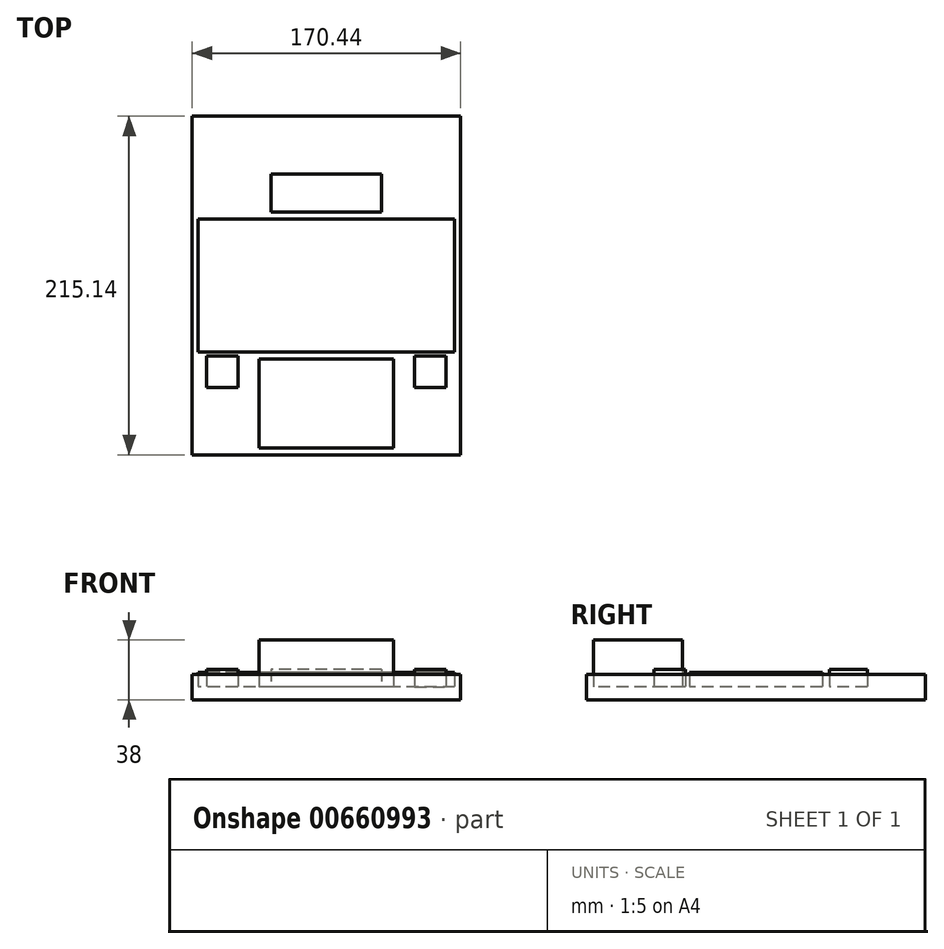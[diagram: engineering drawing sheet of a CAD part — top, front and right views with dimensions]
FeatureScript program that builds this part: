
annotation { "Feature Type Name" : "Feature", "Feature Type Description" : "" }
export const myFeature = defineFeature(function(context is Context, id is Id, definition is map)
    precondition{}
    {
        {
            var Q0;
            Q0=qCreatedBy(makeId("Top.planeOp"),FACE);
            var sketch = newSketch(context, id + "F0", { "sketchPlane" : qUnion([Q0])});
            skLineSegment(sketch, "E0.bottom", {"start": v(81.47, 42.2) * mm, "end": v(-81.47, 42.2) * mm});
            skLineSegment(sketch, "E0.top", {"start": v(81.47, -42.2) * mm, "end": v(-81.47, -42.2) * mm});
            skLineSegment(sketch, "E0.left", {"start": v(81.47, 42.2) * mm, "end": v(81.47, -42.2) * mm});
            skLineSegment(sketch, "E0.right", {"start": v(-81.47, 42.2) * mm, "end": v(-81.47, -42.2) * mm});
            skPoint(sketch, "E0.middle", {"position": v(0, 0) * mm});
            skSolve(sketch);
        }
        {
            var Q0;
            Q0=qCreatedBy(makeId("Top.planeOp"),FACE);
            var sketch = newSketch(context, id + "F1", { "sketchPlane" : qUnion([Q0])});
            skLineSegment(sketch, "E1.bottom", {"start": v(-56.07, -44.77) * mm, "end": v(-76.07, -44.77) * mm});
            skLineSegment(sketch, "E1.top", {"start": v(-56.07, -64.77) * mm, "end": v(-76.07, -64.77) * mm});
            skLineSegment(sketch, "E1.left", {"start": v(-56.07, -44.77) * mm, "end": v(-56.07, -64.77) * mm});
            skLineSegment(sketch, "E1.right", {"start": v(-76.07, -44.77) * mm, "end": v(-76.07, -64.77) * mm});
            skPoint(sketch, "E1.middle", {"position": v(-66.07, -54.77) * mm});
            skSolve(sketch);
        }
        {
            var Q0;
            Q0=qCreatedBy(makeId("Top.planeOp"),FACE);
            var sketch = newSketch(context, id + "F2", { "sketchPlane" : qUnion([Q0])});
            skLineSegment(sketch, "E2.bottom", {"start": v(35.05, 70.7) * mm, "end": v(-35.05, 70.7) * mm});
            skLineSegment(sketch, "E2.top", {"start": v(35.05, 46.7) * mm, "end": v(-35.05, 46.7) * mm});
            skLineSegment(sketch, "E2.left", {"start": v(35.05, 70.7) * mm, "end": v(35.05, 46.7) * mm});
            skLineSegment(sketch, "E2.right", {"start": v(-35.05, 70.7) * mm, "end": v(-35.05, 46.7) * mm});
            skPoint(sketch, "E2.middle", {"position": v(0, 58.7) * mm});
            skSolve(sketch);
        }
        {
            var Q0;
            Q0=makeQuery(id+"F0.imprint","IMPRINT",FACE,{"disambiguationData":[TD([[makeQuery(id+"F0.imprint","IMPRINT",EDGE,{"derivedFrom":sQuery(id+"F0.wireOp",EDGE,"E0.bottom")}),1.0]])]});
            extrude(context, id + "F3", {"entities" : qUnion([Q0]), "depth" : 9.35 * mm, "offsetDistance" : 25 * mm});
        }
        {
            var Q0;
            Q0=makeQuery(id+"F1.imprint","IMPRINT",FACE,{"disambiguationData":[TD([[makeQuery(id+"F1.imprint","IMPRINT",EDGE,{"derivedFrom":sQuery(id+"F1.wireOp",EDGE,"E1.bottom")}),1.0]])]});
            extrude(context, id + "F4", {"entities" : qUnion([Q0]), "depth" : 11.3 * mm, "offsetDistance" : 25 * mm});
        }
        {
            var Q0;
            Q0 = qSketchRegion(id + "F2", true);
            extrude(context, id + "F5", {"entities" : qUnion([Q0]), "depth" : 11.17 * mm, "offsetDistance" : 25 * mm});
        }
        {
            var Q0;
            Q0=makeQuery(id+"F4.opExtrude","SWEPT_BODY",BODY,{"disambiguationData":[OSD([sQuery(id+"F1.wireOp",EDGE,"E1.bottom"),sQuery(id+"F1.wireOp",EDGE,"E1.top"),sQuery(id+"F1.wireOp",EDGE,"E1.left"),sQuery(id+"F1.wireOp",EDGE,"E1.right")])]});
            var Q1;
            Q1=qCreatedBy(makeId("Right.planeOp"),FACE);
            mirror(context, id + "F6", {"entities" : qUnion([Q0]), "mirrorPlane" : qUnion([Q1])});
        }
        {
            var Q0;
            Q0=qCreatedBy(makeId("Top.planeOp"),FACE);
            var sketch = newSketch(context, id + "F7", { "sketchPlane" : qUnion([Q0])});
            skLineSegment(sketch, "E3.bottom", {"start": v(42.8, -46.54) * mm, "end": v(-42.8, -46.54) * mm});
            skLineSegment(sketch, "E3.top", {"start": v(42.8, -103.04) * mm, "end": v(-42.8, -103.04) * mm});
            skLineSegment(sketch, "E3.left", {"start": v(42.8, -46.54) * mm, "end": v(42.8, -103.04) * mm});
            skLineSegment(sketch, "E3.right", {"start": v(-42.8, -46.54) * mm, "end": v(-42.8, -103.04) * mm});
            skPoint(sketch, "E3.middle", {"position": v(0, -74.8) * mm});
            skSolve(sketch);
        }
        {
            var Q0;
            Q0=makeQuery(id+"F7.imprint","IMPRINT",FACE,{"disambiguationData":[TD([[makeQuery(id+"F7.imprint","IMPRINT",EDGE,{"derivedFrom":sQuery(id+"F7.wireOp",EDGE,"E3.bottom")}),1.0]])]});
            extrude(context, id + "F8", {"entities" : qUnion([Q0]), "depth" : 30 * mm, "offsetDistance" : 25 * mm});
        }
        {
            var Q0;
            Q0=qCreatedBy(makeId("Top.planeOp"),FACE);
            var sketch = newSketch(context, id + "F9", { "sketchPlane" : qUnion([Q0])});
            skLineSegment(sketch, "E4.bottom", {"start": v(85.22, -107.57) * mm, "end": v(-85.22, -107.57) * mm});
            skLineSegment(sketch, "E4.top", {"start": v(85.22, 107.57) * mm, "end": v(-85.22, 107.57) * mm});
            skLineSegment(sketch, "E4.left", {"start": v(85.22, -107.57) * mm, "end": v(85.22, 107.57) * mm});
            skLineSegment(sketch, "E4.right", {"start": v(-85.22, -107.57) * mm, "end": v(-85.22, 107.57) * mm});
            skPoint(sketch, "E4.middle", {"position": v(0, 0) * mm});
            skSolve(sketch);
        }
        {
            var Q0;
            Q0=makeQuery(id+"F9.imprint","IMPRINT",FACE,{"disambiguationData":[TD([[makeQuery(id+"F9.imprint","IMPRINT",EDGE,{"derivedFrom":sQuery(id+"F9.wireOp",EDGE,"E4.bottom")}),-1.0]])]});
            extrude(context, id + "F10", {"entities" : qUnion([Q0]), "endBound" : BoundingType.SYMMETRIC, "depth" : 16 * mm, "offsetDistance" : 25 * mm});
        }
    });
